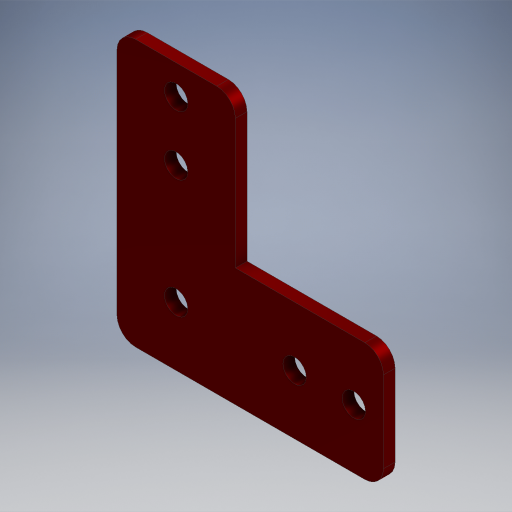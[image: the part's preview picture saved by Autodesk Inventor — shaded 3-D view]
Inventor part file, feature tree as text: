
AUTODESK INVENTOR PART (.ipt)
format: ipt  version: 2024.2 (Build 282272000, 272)  size: 320,512 bytes
history: native  units: in
note: dims shown in document units (in); Inventor stores cm internally (conversion verified against a paired STEP export)
features: extrude x1, fillet x1, sketch x1, projected_geometry x1, other x1
ambient origin geometry x8: Origin, YZ Plane, XZ Plane, XY Plane, X Axis, Y Axis, Z Axis, Center Point
bodies: Solid1 (feature_tree)
feature tree (5):
  extrude  "Extrusion1"  Depth=0.157in
  fillet  "Fillet1"  Radius=1.0in
  sketch  "Sketch1"  dims[d0=0.5in d1=0.5in d2=1.0in d3=0.0in d4=0.157in]
  projected_geometry  "Projected Loop1"
  other  "TTB-0082 - Aluminum L Gusset - 5mm Hole Size"
